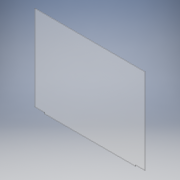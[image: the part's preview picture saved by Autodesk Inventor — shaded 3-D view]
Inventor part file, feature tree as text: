
AUTODESK INVENTOR PART (.ipt)
format: ipt  version: 2018 (Build 220112000, 112)  size: 201,728 bytes
history: native  units: in
note: dims shown in document units (in); Inventor stores cm internally (conversion verified against a paired STEP export)
features: extrude x4, sketch x4, imported_body x1
ambient origin geometry x8: Origin, YZ Plane, XZ Plane, XY Plane, X Axis, Y Axis, Z Axis, Center Point
bodies: Solid1 (feature_tree)
feature tree (9):
  extrude  "Extrusion1"  Depth=7.4803in TaperAngle=0.0deg
  extrude  "Extrusion2"  Depth=2.1496in
  extrude  "Extrusion3"  Depth=39.3701in TaperAngle=0.0deg
  extrude  "Extrusion4"  [1 undecoded]
  sketch  "Sketch1"  dims[d0=3.7795in d1=7.4803in d2=0.0in]
  sketch  "Sketch2"  dims[d3=7.4803in d4=0.0in d7=2.1496in]
  sketch  "Sketch3"  dims[d8=0.1969in d9=0.0in d10=39.3701in d11=0.0in]
  sketch  "Sketch5"
  imported_body  "Imported1"
note: 1 required parameter value undecoded (feature->parameter linkage not recoverable at this tier; creation-order binding heuristic only, values carry confidence <= 0.55)
